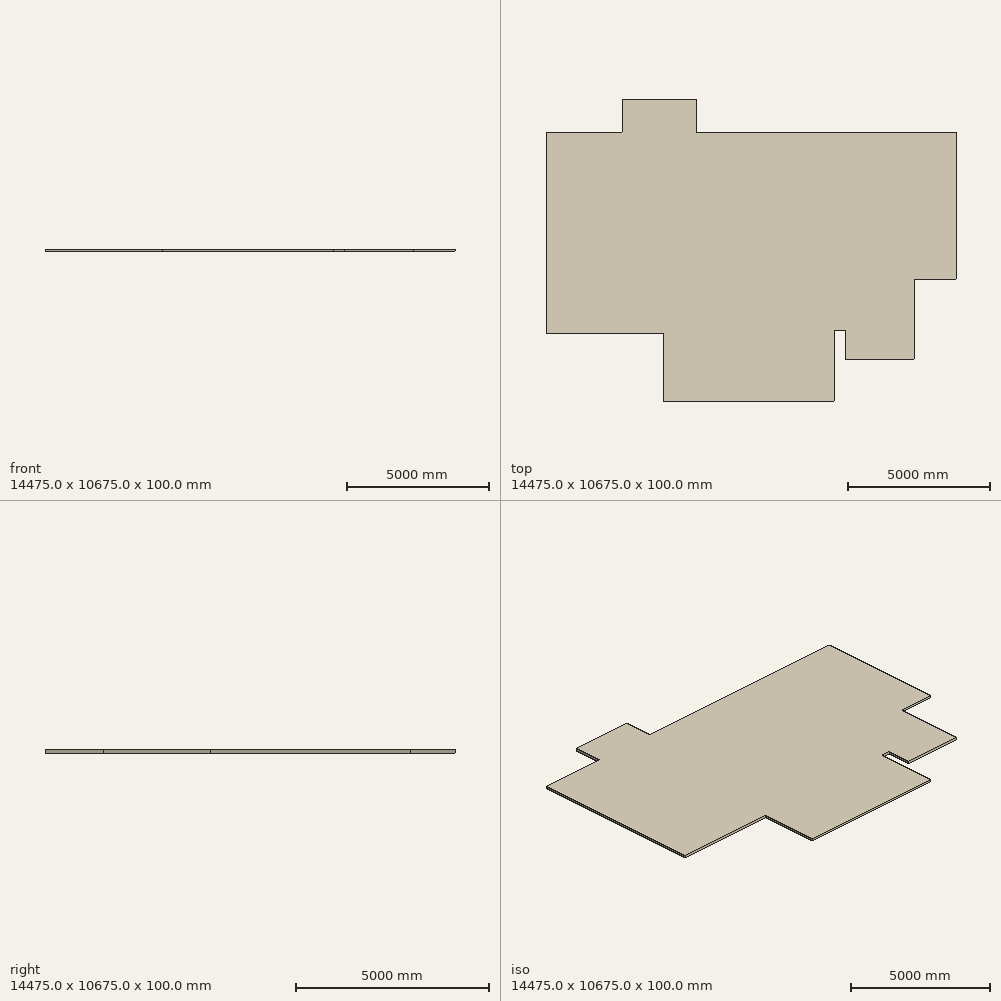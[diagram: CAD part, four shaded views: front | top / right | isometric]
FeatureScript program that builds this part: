
annotation { "Feature Type Name" : "Feature", "Feature Type Description" : "" }
export const myFeature = defineFeature(function(context is Context, id is Id, definition is map)
    precondition{}
    {
        {
            var Q0;
            Q0=qCreatedBy(makeId("Top.planeOp"),FACE);
            var sketch = newSketch(context, id + "F0", { "sketchPlane" : qUnion([Q0])});
            skLineSegment(sketch, "E0", {"start": v(-3.72, -162.63) * mm, "end": v(-4128.72, -162.63) * mm});
            skLineSegment(sketch, "E1", {"start": v(-4128.72, -162.63) * mm, "end": v(-4128.72, 6937.37) * mm});
            skLineSegment(sketch, "E2", {"start": v(-4128.72, 6937.37) * mm, "end": v(-1428.72, 6937.37) * mm});
            skLineSegment(sketch, "E3", {"start": v(-1428.72, 6937.37) * mm, "end": v(-1428.72, 8112.37) * mm});
            skLineSegment(sketch, "E4", {"start": v(-1428.72, 8112.37) * mm, "end": v(1171.28, 8112.37) * mm});
            skLineSegment(sketch, "E5", {"start": v(1171.28, 8112.37) * mm, "end": v(1171.28, 6937.37) * mm});
            skLineSegment(sketch, "E6", {"start": v(1171.28, 6937.37) * mm, "end": v(10346.28, 6937.37) * mm});
            skLineSegment(sketch, "E7", {"start": v(10346.28, 6937.37) * mm, "end": v(10346.28, 1737.37) * mm});
            skLineSegment(sketch, "E8", {"start": v(10346.28, 1737.37) * mm, "end": v(8871.28, 1737.37) * mm});
            skLineSegment(sketch, "E9", {"start": v(8871.28, 1737.37) * mm, "end": v(8871.28, -1062.63) * mm});
            skLineSegment(sketch, "E10", {"start": v(8871.28, -1062.63) * mm, "end": v(6421.28, -1062.63) * mm});
            skLineSegment(sketch, "E11", {"start": v(6046.28, -1062.63) * mm, "end": v(6046.28, -2562.63) * mm});
            skLineSegment(sketch, "E12", {"start": v(6046.28, -2562.63) * mm, "end": v(-3.72, -2562.63) * mm});
            skLineSegment(sketch, "E13", {"start": v(-3.72, -2562.63) * mm, "end": v(-3.72, -162.63) * mm});
            skLineSegment(sketch, "E14", {"start": v(6421.28, -1062.63) * mm, "end": v(6421.28, -162.63) * mm});
            skLineSegment(sketch, "E15", {"start": v(6046.28, -162.63) * mm, "end": v(6046.28, -1062.63) * mm});
            skLineSegment(sketch, "E16", {"start": v(6046.28, -162.63) * mm, "end": v(6046.28, -62.63) * mm});
            skLineSegment(sketch, "E17", {"start": v(6046.28, -62.63) * mm, "end": v(6421.28, -62.63) * mm});
            skLineSegment(sketch, "E18", {"start": v(6421.28, -62.63) * mm, "end": v(6421.28, -162.63) * mm});
            skSolve(sketch);
        }
        {
            var Q0;
            Q0=qSketchRegion(id+"F0",true);
            extrude(context, id + "F1", {"entities" : qUnion([Q0]), "depth" : 100 * mm});
        }
    });
